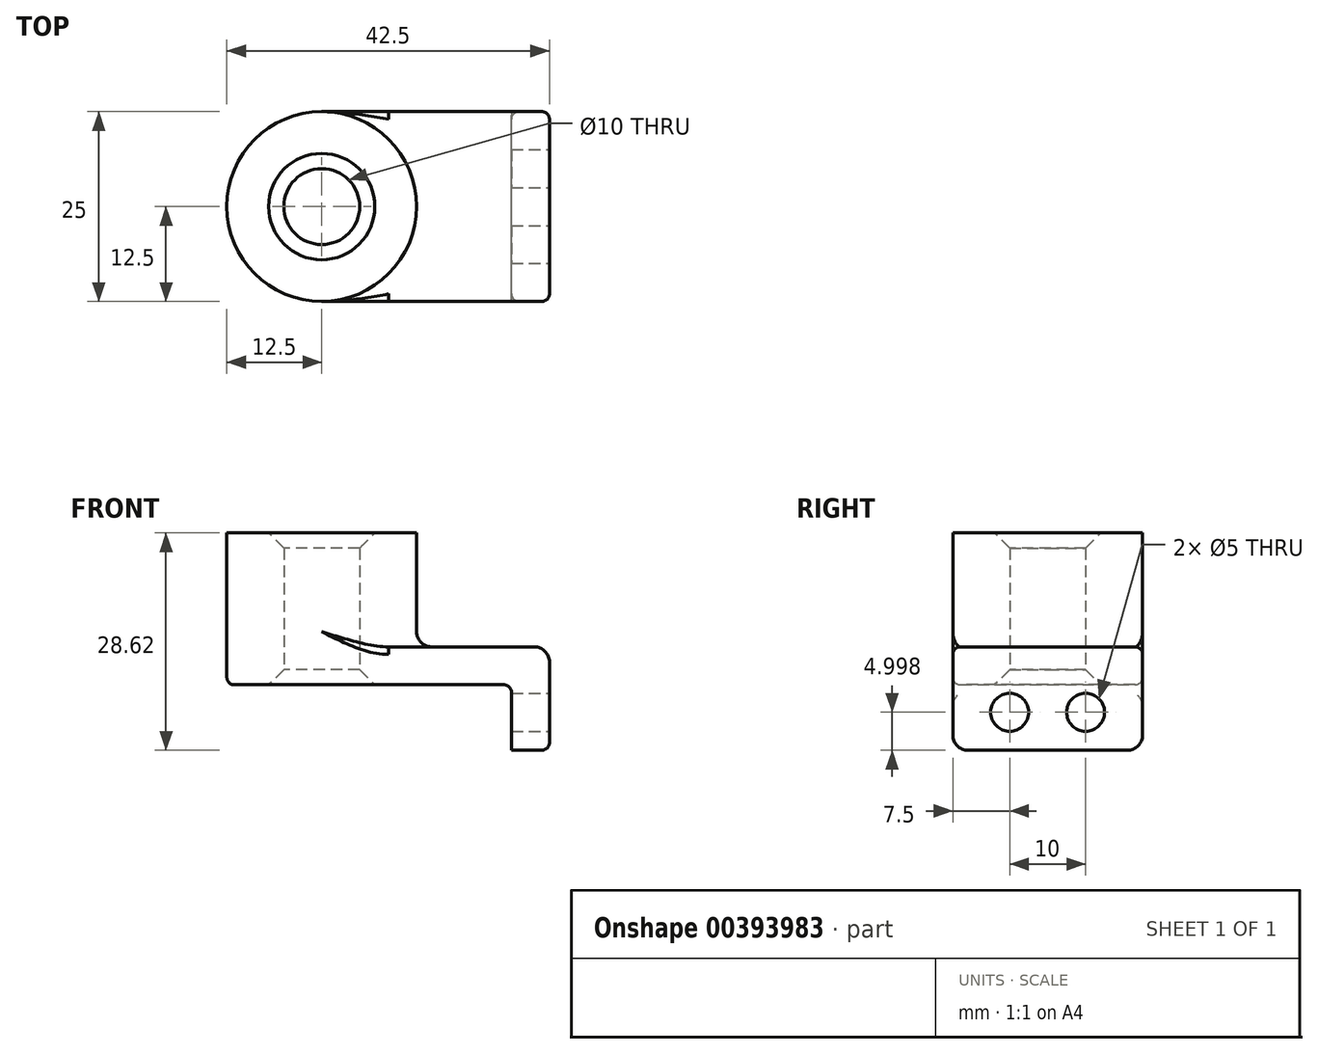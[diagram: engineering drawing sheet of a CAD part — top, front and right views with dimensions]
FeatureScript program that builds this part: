
annotation { "Feature Type Name" : "Feature", "Feature Type Description" : "" }
export const myFeature = defineFeature(function(context is Context, id is Id, definition is map)
    precondition{}
    {
        {
            var Q0;
            Q0=qCreatedBy(makeId("Top.planeOp"),FACE);
            var sketch = newSketch(context, id + "F0", { "sketchPlane" : qUnion([Q0])});
            skLineSegment(sketch, "E0.bottom", {"start": v(15, -12.5) * mm, "end": v(-15, -12.5) * mm});
            skLineSegment(sketch, "E0.top", {"start": v(15, 12.5) * mm, "end": v(-15, 12.5) * mm});
            skLineSegment(sketch, "E0.left", {"start": v(15, -12.5) * mm, "end": v(15, 12.5) * mm});
            skLineSegment(sketch, "E0.right", {"start": v(-15, -12.5) * mm, "end": v(-15, 12.5) * mm});
            skPoint(sketch, "E0.middle", {"position": v(0, 0) * mm});
            skCircle(sketch, "E1", {"center": v(-15, 0) * mm, "radius": 12.5 * mm});
            skCircle(sketch, "E2", {"center": v(-15, 0) * mm, "radius": 5 * mm});
            skSolve(sketch);
        }
        {
            var Q0;
            {var subQ0=sQuery(id+"F0.wireOp",EDGE,"E0.bottom");Q0=makeQuery(id+"F0.imprint","IMPRINT",FACE,{"disambiguationData":[TD([[makeQuery(id+"F0.imprint","IMPRINT",EDGE,{"derivedFrom":subQ0}),-1.0]])]});}
            var Q1;
            {var subQ1=sQuery(id+"F0.wireOp",EDGE,"E0.right");var subQ3=sQuery(id+"F0.wireOp",EDGE,"E2");var subQ4=makeQuery(id+"F0.imprint","INTERSECT",VERTEX,{"disambiguationData":[OD(0.0)],"derivedFrom":[subQ1,subQ3]});Q1=makeQuery(id+"F0.imprint","IMPRINT",FACE,{"disambiguationData":[TD([[makeQuery(id+"F0.imprint","IMPRINT",EDGE,{"disambiguationData":[TD([[subQ4,-1.0]])],"derivedFrom":subQ3}),-1.0]])]});}
            var Q2;
            {var subQ1=sQuery(id+"F0.wireOp",EDGE,"E0.right");var subQ3=sQuery(id+"F0.wireOp",EDGE,"E2");var subQ4=makeQuery(id+"F0.imprint","INTERSECT",VERTEX,{"disambiguationData":[OD(0.0)],"derivedFrom":[subQ1,subQ3]});Q2=makeQuery(id+"F0.imprint","IMPRINT",FACE,{"disambiguationData":[TD([[makeQuery(id+"F0.imprint","IMPRINT",EDGE,{"disambiguationData":[TD([[subQ4,1.0]])],"derivedFrom":subQ3}),-1.0]])]});}
            var Q3;
            Q3 = qSketchRegion(id + "F0", true);
            extrude(context, id + "F1", {"entities" : qUnion([Q0, Q1, Q2, Q3]), "depth" : 5 * mm});
        }
        {
            var Q0;
            {var subQ1=sQuery(id+"F0.wireOp",EDGE,"E0.right");var subQ3=sQuery(id+"F0.wireOp",EDGE,"E2");var subQ4=makeQuery(id+"F0.imprint","INTERSECT",VERTEX,{"disambiguationData":[OD(0.0)],"derivedFrom":[subQ1,subQ3]});Q0=makeQuery(id+"F0.imprint","IMPRINT",FACE,{"disambiguationData":[TD([[makeQuery(id+"F0.imprint","IMPRINT",EDGE,{"disambiguationData":[TD([[subQ4,1.0]])],"derivedFrom":subQ3}),-1.0]])]});}
            var Q1;
            {var subQ1=sQuery(id+"F0.wireOp",EDGE,"E0.right");var subQ3=sQuery(id+"F0.wireOp",EDGE,"E2");var subQ4=makeQuery(id+"F0.imprint","INTERSECT",VERTEX,{"disambiguationData":[OD(0.0)],"derivedFrom":[subQ1,subQ3]});Q1=makeQuery(id+"F0.imprint","IMPRINT",FACE,{"disambiguationData":[TD([[makeQuery(id+"F0.imprint","IMPRINT",EDGE,{"disambiguationData":[TD([[subQ4,-1.0]])],"derivedFrom":subQ3}),-1.0]])]});}
            extrude(context, id + "F2", {"entities" : qUnion([Q0, Q1]), "operationType" : NewBodyOperationType.ADD, "depth" : 20 * mm});
        }
        {
            var Q0;
            Q0=makeQuery(id+"F1.opExtrude","SWEPT_FACE",FACE,{"disambiguationData":[OSD([sQuery(id+"F0.wireOp",EDGE,"E0.left")])]});
            var sketch = newSketch(context, id + "F3", { "sketchPlane" : qUnion([Q0])});
            skLineSegment(sketch, "E3.bottom", {"start": v(-12.5, 5) * mm, "end": v(12.5, 5) * mm});
            skLineSegment(sketch, "E3.top", {"start": v(-12.5, -8.62) * mm, "end": v(12.5, -8.62) * mm});
            skLineSegment(sketch, "E3.left", {"start": v(-12.5, 5) * mm, "end": v(-12.5, -8.62) * mm});
            skLineSegment(sketch, "E3.right", {"start": v(12.5, 5) * mm, "end": v(12.5, -8.62) * mm});
            skCircle(sketch, "E4", {"center": v(-5, -3.62) * mm, "radius": 2.5 * mm});
            skLineSegment(sketch, "E5", {"start": v(0, 5) * mm, "end": v(0, -8.62) * mm, "construction": true});
            skCircle(sketch, "E6.MirrorC", {"center": v(5, -3.62) * mm, "radius": 2.5 * mm});
            skSolve(sketch);
        }
        {
            var Q0;
            {var subQ2=sQuery(id+"F3.wireOp",EDGE,"E3.top");Q0=makeQuery(id+"F3.imprint","IMPRINT",FACE,{"disambiguationData":[TD([[makeQuery(id+"F3.imprint","IMPRINT",EDGE,{"derivedFrom":subQ2}),1.0]])]});}
            var Q1;
            {var subQ0=sQuery(id+"F3.wireOp",EDGE,"E3.bottom");Q1=makeQuery(id+"F3.imprint","IMPRINT",FACE,{"disambiguationData":[TD([[makeQuery(id+"F3.imprint","IMPRINT",EDGE,{"derivedFrom":subQ0}),-1.0]])]});}
            extrude(context, id + "F4", {"entities" : qUnion([Q0, Q1]), "operationType" : NewBodyOperationType.ADD, "oppositeDirection" : true, "depth" : 5 * mm});
        }
        {
            var Q0;
            {var subQ0=sQuery(id+"F0.wireOp",EDGE,"E1");Q0=makeQuery(id+"F2.boolean.opBoolean","INTERSECT",EDGE,{"derivedFrom":[makeQuery(id+"F1.opExtrude","CAP_FACE",FACE,{"disambiguationData":[OSD([sQuery(id+"F0.wireOp",EDGE,"E0.bottom"),sQuery(id+"F0.wireOp",EDGE,"E0.top"),sQuery(id+"F0.wireOp",EDGE,"E0.left"),subQ0,sQuery(id+"F0.wireOp",EDGE,"E2")])],"isStart":false}),makeQuery(id+"F2.opExtrude","SWEPT_FACE",FACE,{"disambiguationData":[OSD([subQ0])]})]});}
            var Q1;
            Q1=makeQuery(id+"F1.opExtrude","CAP_EDGE",EDGE,{"disambiguationData":[OSD([sQuery(id+"F0.wireOp",EDGE,"E0.left")])],"isStart":false});
            var Q2;
            Q2=makeQuery(id+"F4.opExtrude","SWEPT_EDGE",EDGE,{"disambiguationData":[OSD([sQuery(id+"F3.wireOp",EDGE,"E3.top"),sQuery(id+"F3.wireOp",EDGE,"E3.left")])]});
            var Q3;
            Q3=makeQuery(id+"F4.opExtrude","SWEPT_EDGE",EDGE,{"disambiguationData":[OSD([sQuery(id+"F3.wireOp",EDGE,"E3.top"),sQuery(id+"F3.wireOp",EDGE,"E3.right")])]});
            fillet(context, id + "F5", {"entities" : qUnion([Q0, Q1, Q2, Q3]), "radius" : 2 * mm, "tangentPropagation" : true, "allowEdgeOverflow" : false});
        }
        {
            var Q0;
            Q0=makeQuery(id+"F1.opExtrude","CAP_EDGE",EDGE,{"disambiguationData":[OSD([sQuery(id+"F0.wireOp",EDGE,"E0.bottom")])],"isStart":false});
            var Q1;
            Q1=makeQuery(id+"F1.opExtrude","CAP_EDGE",EDGE,{"disambiguationData":[OSD([sQuery(id+"F0.wireOp",EDGE,"E0.bottom")])],"isStart":true});
            var Q2;
            Q2=makeQuery(id+"F4.boolean.opBoolean","INTERSECT",EDGE,{"derivedFrom":[makeQuery(id+"F1.opExtrude","CAP_FACE",FACE,{"disambiguationData":[OSD([sQuery(id+"F0.wireOp",EDGE,"E0.bottom"),sQuery(id+"F0.wireOp",EDGE,"E0.top"),sQuery(id+"F0.wireOp",EDGE,"E0.left"),sQuery(id+"F0.wireOp",EDGE,"E1"),sQuery(id+"F0.wireOp",EDGE,"E2")])],"isStart":true}),makeQuery(id+"F4.opExtrude","CAP_FACE",FACE,{"disambiguationData":[OSD([sQuery(id+"F3.wireOp",EDGE,"E3.bottom"),sQuery(id+"F3.wireOp",EDGE,"E3.top"),sQuery(id+"F3.wireOp",EDGE,"E3.left"),sQuery(id+"F3.wireOp",EDGE,"E3.right"),sQuery(id+"F3.wireOp",EDGE,"E4"),sQuery(id+"F3.wireOp",EDGE,"E6.MirrorC")])],"isStart":false})]});
            fillet(context, id + "F6", {"entities" : qUnion([Q0, Q1, Q2]), "radius" : 1 * mm, "tangentPropagation" : true, "allowEdgeOverflow" : false});
        }
        {
            var Q0;
            {var subQ0=sQuery(id+"F0.wireOp",EDGE,"E2");Q0=makeQuery(id+"F2.boolean.opBoolean","MERGE",FACE,{"derivedFrom":[makeQuery(id+"F1.opExtrude","SWEPT_FACE",FACE,{"disambiguationData":[OSD([subQ0])]}),makeQuery(id+"F2.opExtrude","SWEPT_FACE",FACE,{"disambiguationData":[OSD([subQ0])]})]});}
            chamfer(context, id + "F7", {"entities" : qUnion([Q0]), "width" : 2 * mm, "tangentPropagation" : true});
        }
    });
